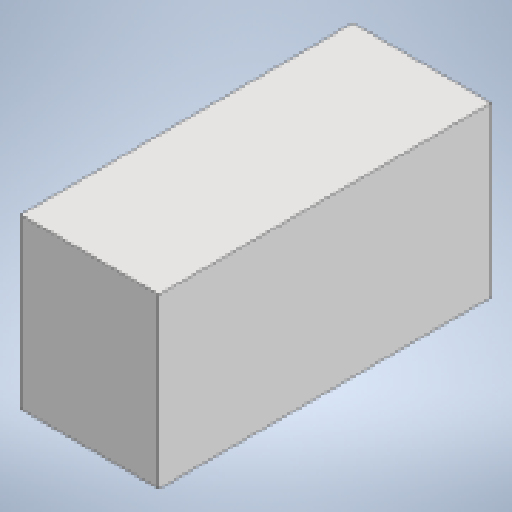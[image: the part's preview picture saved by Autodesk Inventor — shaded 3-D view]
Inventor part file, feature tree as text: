
AUTODESK INVENTOR PART (.ipt)
format: ipt  version: 2023 (Build 270158000, 158)  size: 124,416 bytes
history: native  units: mm
features: extrude x2, sketch x2, projected_geometry x1
ambient origin geometry x8: Origin, YZ Plane, XZ Plane, XY Plane, X Axis, Y Axis, Z Axis, Center Point
bodies: Solid1 (feature_tree)
feature tree (5):
  extrude  "Extrusion1"  Depth=25.0mm
  extrude  "Extrusion2"  Depth=30.4mm
  sketch  "Sketch1"  dims[d0=60.0mm d1=25.0mm]
  sketch  "Sketch2"  dims[d2=13.0mm d3=46.0mm d4=6.0mm d5=30.4mm d6=0.0mm d7=2.917mm d8=0.0mm]
  projected_geometry  "Projected Loop1"
